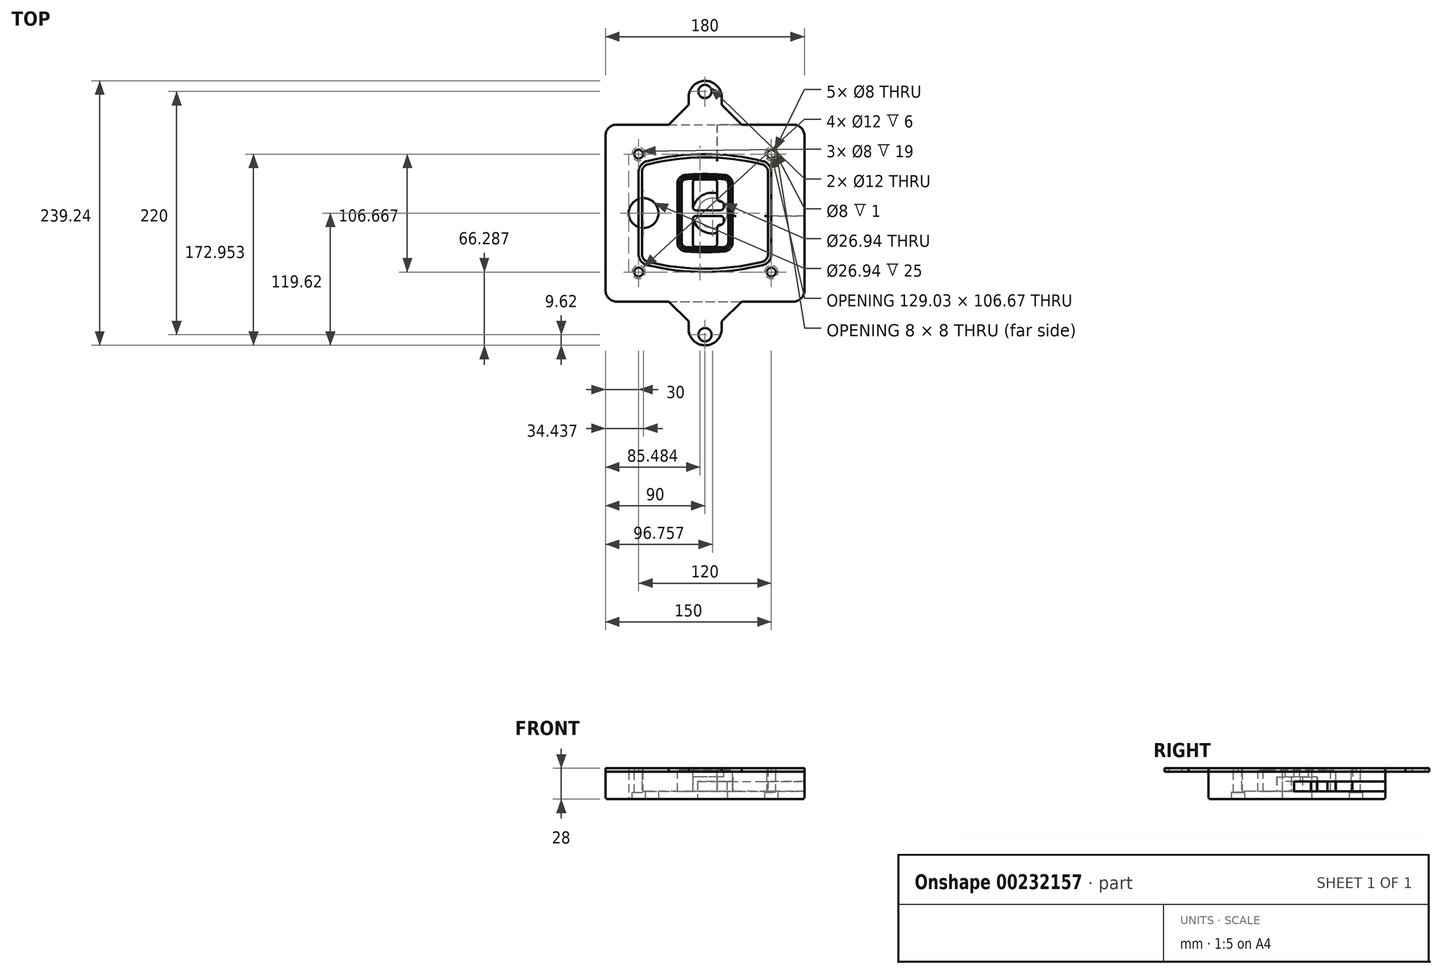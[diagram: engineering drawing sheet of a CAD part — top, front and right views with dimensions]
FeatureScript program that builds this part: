
annotation { "Feature Type Name" : "Feature", "Feature Type Description" : "" }
export const myFeature = defineFeature(function(context is Context, id is Id, definition is map)
    precondition{}
    {
        {
            var Q0;
            Q0=qCreatedBy(makeId("Top.planeOp"),FACE);
            var sketch = newSketch(context, id + "F0", { "sketchPlane" : qUnion([Q0])});
            skPoint(sketch, "E0.rect.middle", {"position": v(0, 0) * mm});
            skLineSegment(sketch, "E1.bottom", {"start": v(-80, -80) * mm, "end": v(80, -80) * mm});
            skLineSegment(sketch, "E1.top", {"start": v(-80, 80) * mm, "end": v(80, 80) * mm});
            skLineSegment(sketch, "E1.left", {"start": v(-90, -70) * mm, "end": v(-90, 70) * mm});
            skLineSegment(sketch, "E1.right", {"start": v(90, -70) * mm, "end": v(90, 70) * mm});
            skLineSegment(sketch, "E2", {"start": v(-90, 80) * mm, "end": v(90, -80) * mm, "construction": true});
            skLineSegment(sketch, "E3", {"start": v(90, 80) * mm, "end": v(-90, -80) * mm, "construction": true});
            skCircle(sketch, "E4", {"center": v(-60, 53.33) * mm, "radius": 4 * mm});
            skCircle(sketch, "E5", {"center": v(60, 53.33) * mm, "radius": 4 * mm});
            skCircle(sketch, "E6", {"center": v(60, -53.33) * mm, "radius": 4 * mm});
            skCircle(sketch, "E7", {"center": v(-60, -53.33) * mm, "radius": 4 * mm});
            skLineSegment(sketch, "E8", {"start": v(-60, 53.33) * mm, "end": v(60, 53.33) * mm, "construction": true});
            skLineSegment(sketch, "E9", {"start": v(60, 53.33) * mm, "end": v(60, -53.33) * mm, "construction": true});
            skLineSegment(sketch, "E10", {"start": v(60, -53.33) * mm, "end": v(-60, -53.33) * mm, "construction": true});
            skLineSegment(sketch, "E11", {"start": v(-60, -53.33) * mm, "end": v(-60, 53.33) * mm, "construction": true});
            skLineSegment(sketch, "E12", {"start": v(-60, 37.3) * mm, "end": v(-60, -37.3) * mm});
            skLineSegment(sketch, "E13", {"start": v(60, 37.3) * mm, "end": v(60, -37.3) * mm});
            skArc(sketch, "E14", {"start": v(52.38, 47.01) * mm, "mid": v(0, 53.33) * mm, "end": v(-52.38, 47.01) * mm});
            skArc(sketch, "E15", {"start": v(-52.38, -47.01) * mm, "mid": v(0, -53.33) * mm, "end": v(52.38, -47.01) * mm});
            skLineSegment(sketch, "E16", {"start": v(-60, 0) * mm, "end": v(60, 0) * mm, "construction": true});
            skPoint(sketch, "E17.visualSharp", {"position": v(-60, -45) * mm});
            skArc(sketch, "E17.filletArc", {"start": v(-60, -37.3) * mm, "mid": v(-57.87, -43.47) * mm, "end": v(-52.38, -47.01) * mm});
            skPoint(sketch, "E18.visualSharp", {"position": v(-60, 45) * mm});
            skArc(sketch, "E18.filletArc", {"start": v(-52.38, 47.01) * mm, "mid": v(-57.87, 43.47) * mm, "end": v(-60, 37.3) * mm});
            skPoint(sketch, "E19.visualSharp", {"position": v(60, 45) * mm});
            skArc(sketch, "E19.filletArc", {"start": v(60, 37.3) * mm, "mid": v(57.87, 43.47) * mm, "end": v(52.38, 47.01) * mm});
            skPoint(sketch, "E20.visualSharp", {"position": v(60, -45) * mm});
            skArc(sketch, "E20.filletArc", {"start": v(52.38, -47.01) * mm, "mid": v(57.87, -43.47) * mm, "end": v(60, -37.3) * mm});
            skPoint(sketch, "E21.visualSharp", {"position": v(-90, 80) * mm});
            skArc(sketch, "E21.filletArc", {"start": v(-80, 80) * mm, "mid": v(-87.07, 77.07) * mm, "end": v(-90, 70) * mm});
            skPoint(sketch, "E22.visualSharp", {"position": v(90, 80) * mm});
            skArc(sketch, "E22.filletArc", {"start": v(90, 70) * mm, "mid": v(87.07, 77.07) * mm, "end": v(80, 80) * mm});
            skPoint(sketch, "E23.visualSharp", {"position": v(90, -80) * mm});
            skArc(sketch, "E23.filletArc", {"start": v(80, -80) * mm, "mid": v(87.07, -77.07) * mm, "end": v(90, -70) * mm});
            skPoint(sketch, "E24.visualSharp", {"position": v(-90, -80) * mm});
            skArc(sketch, "E24.filletArc", {"start": v(-90, -70) * mm, "mid": v(-87.07, -77.07) * mm, "end": v(-80, -80) * mm});
            skArc(sketch, "E25.0", {"start": v(57, 37.3) * mm, "mid": v(55.5, 41.62) * mm, "end": v(51.67, 44.1) * mm});
            skLineSegment(sketch, "E25.1", {"start": v(57, 37.3) * mm, "end": v(57, -37.3) * mm});
            skArc(sketch, "E25.2", {"start": v(51.67, -44.1) * mm, "mid": v(55.5, -41.62) * mm, "end": v(57, -37.3) * mm});
            skArc(sketch, "E25.3", {"start": v(-51.67, -44.1) * mm, "mid": v(0, -50.33) * mm, "end": v(51.67, -44.1) * mm});
            skArc(sketch, "E25.4", {"start": v(-57, -37.3) * mm, "mid": v(-55.5, -41.62) * mm, "end": v(-51.67, -44.1) * mm});
            skArc(sketch, "E25.5", {"start": v(51.67, 44.1) * mm, "mid": v(0, 50.33) * mm, "end": v(-51.67, 44.1) * mm});
            skLineSegment(sketch, "E25.6", {"start": v(-57, 37.3) * mm, "end": v(-57, -37.3) * mm});
            skArc(sketch, "E25.7", {"start": v(-51.67, 44.1) * mm, "mid": v(-55.5, 41.62) * mm, "end": v(-57, 37.3) * mm});
            skArc(sketch, "E26.0", {"start": v(-53.33, 50.9) * mm, "mid": v(-61.01, 45.94) * mm, "end": v(-64, 37.3) * mm});
            skArc(sketch, "E26.1", {"start": v(53.33, 50.9) * mm, "mid": v(0, 57.33) * mm, "end": v(-53.33, 50.9) * mm});
            skArc(sketch, "E26.2", {"start": v(64, 37.3) * mm, "mid": v(61.01, 45.94) * mm, "end": v(53.33, 50.9) * mm});
            skLineSegment(sketch, "E26.3", {"start": v(64, 37.3) * mm, "end": v(64, -37.3) * mm});
            skArc(sketch, "E26.4", {"start": v(53.33, -50.9) * mm, "mid": v(61.01, -45.94) * mm, "end": v(64, -37.3) * mm});
            skLineSegment(sketch, "E26.5", {"start": v(-64, 37.3) * mm, "end": v(-64, -37.3) * mm});
            skArc(sketch, "E26.6", {"start": v(-53.33, -50.9) * mm, "mid": v(0, -57.33) * mm, "end": v(53.33, -50.9) * mm});
            skArc(sketch, "E26.7", {"start": v(-64, -37.3) * mm, "mid": v(-61.01, -45.94) * mm, "end": v(-53.33, -50.9) * mm});
            skSolve(sketch);
        }
        {
            var Q0;
            Q0=makeQuery(id+"F0.imprint","IMPRINT",FACE,{"disambiguationData":[TD([[makeQuery(id+"F0.imprint","IMPRINT",EDGE,{"derivedFrom":sQuery(id+"F0.wireOp",EDGE,"E1.bottom")}),1.0]])]});
            var Q1;
            Q1=makeQuery(id+"F0.imprint","IMPRINT",FACE,{"disambiguationData":[TD([[makeQuery(id+"F0.imprint","IMPRINT",EDGE,{"derivedFrom":sQuery(id+"F0.wireOp",EDGE,"E12")}),1.0]])]});
            var Q2;
            Q2=makeQuery(id+"F0.imprint","IMPRINT",FACE,{"disambiguationData":[TD([[makeQuery(id+"F0.imprint","IMPRINT",EDGE,{"derivedFrom":sQuery(id+"F0.wireOp",EDGE,"E25.0")}),1.0]])]});
            var Q3;
            Q3=makeQuery(id+"F0.imprint","IMPRINT",FACE,{"disambiguationData":[TD([[makeQuery(id+"F0.imprint","IMPRINT",EDGE,{"derivedFrom":sQuery(id+"F0.wireOp",EDGE,"E12")}),-1.0]])]});
            extrude(context, id + "F1", {"entities" : qUnion([Q0, Q1, Q2, Q3]), "oppositeDirection" : true, "depth" : 25 * mm});
        }
        {
            var Q0;
            Q0=makeQuery(id+"F0.imprint","IMPRINT",FACE,{"disambiguationData":[TD([[makeQuery(id+"F0.imprint","IMPRINT",EDGE,{"derivedFrom":sQuery(id+"F0.wireOp",EDGE,"E12")}),1.0]])]});
            extrude(context, id + "F2", {"entities" : qUnion([Q0]), "operationType" : NewBodyOperationType.ADD, "depth" : 3 * mm});
        }
        {
            var Q0;
            Q0=makeQuery(id+"F0.imprint","IMPRINT",FACE,{"disambiguationData":[TD([[makeQuery(id+"F0.imprint","IMPRINT",EDGE,{"derivedFrom":sQuery(id+"F0.wireOp",EDGE,"E25.0")}),1.0]])]});
            extrude(context, id + "F3", {"entities" : qUnion([Q0]), "operationType" : NewBodyOperationType.REMOVE, "oppositeDirection" : true, "depth" : 18 * mm});
        }
        {
            var Q0;
            Q0=makeQuery(id+"F2.opExtrude","CAP_FACE",FACE,{"disambiguationData":[OSD([sQuery(id+"F0.wireOp",EDGE,"E12"),sQuery(id+"F0.wireOp",EDGE,"E13"),sQuery(id+"F0.wireOp",EDGE,"E14"),sQuery(id+"F0.wireOp",EDGE,"E15"),sQuery(id+"F0.wireOp",EDGE,"E17.filletArc"),sQuery(id+"F0.wireOp",EDGE,"E18.filletArc"),sQuery(id+"F0.wireOp",EDGE,"E19.filletArc"),sQuery(id+"F0.wireOp",EDGE,"E20.filletArc"),sQuery(id+"F0.wireOp",EDGE,"E25.0"),sQuery(id+"F0.wireOp",EDGE,"E25.1"),sQuery(id+"F0.wireOp",EDGE,"E25.2"),sQuery(id+"F0.wireOp",EDGE,"E25.3"),sQuery(id+"F0.wireOp",EDGE,"E25.4"),sQuery(id+"F0.wireOp",EDGE,"E25.5"),sQuery(id+"F0.wireOp",EDGE,"E25.6"),sQuery(id+"F0.wireOp",EDGE,"E25.7")])],"isStart":false});
            var sketch = newSketch(context, id + "F4", { "sketchPlane" : qUnion([Q0])});
            skArc(sketch, "E27.0", {"start": v(-17.7, -34.56) * mm, "mid": v(0, -35.33) * mm, "end": v(17.7, -34.56) * mm});
            skArc(sketch, "E28.0", {"start": v(17.7, 34.56) * mm, "mid": v(0, 35.33) * mm, "end": v(-17.7, 34.56) * mm});
            skLineSegment(sketch, "E29", {"start": v(-25, 26.59) * mm, "end": v(-25, -26.59) * mm});
            skLineSegment(sketch, "E30", {"start": v(25, 26.59) * mm, "end": v(25, -26.59) * mm});
            skLineSegment(sketch, "E31", {"start": v(-25, 33.78) * mm, "end": v(25, 33.78) * mm, "construction": true});
            skLineSegment(sketch, "E32", {"start": v(-25, -33.78) * mm, "end": v(25, -33.78) * mm, "construction": true});
            skPoint(sketch, "E33.visualSharp", {"position": v(-25, 33.78) * mm});
            skArc(sketch, "E33.filletArc", {"start": v(-17.7, 34.56) * mm, "mid": v(-22.9, 32) * mm, "end": v(-25, 26.59) * mm});
            skPoint(sketch, "E34.visualSharp", {"position": v(25, 33.78) * mm});
            skArc(sketch, "E34.filletArc", {"start": v(25, 26.59) * mm, "mid": v(22.9, 32) * mm, "end": v(17.7, 34.56) * mm});
            skPoint(sketch, "E35.visualSharp", {"position": v(25, -33.78) * mm});
            skArc(sketch, "E35.filletArc", {"start": v(17.7, -34.56) * mm, "mid": v(22.9, -32) * mm, "end": v(25, -26.59) * mm});
            skPoint(sketch, "E36.visualSharp", {"position": v(-25, -33.78) * mm});
            skArc(sketch, "E36.filletArc", {"start": v(-25, -26.59) * mm, "mid": v(-22.9, -32) * mm, "end": v(-17.7, -34.56) * mm});
            skArc(sketch, "E37.0", {"start": v(51.67, 44.1) * mm, "mid": v(0, 50.33) * mm, "end": v(-51.67, 44.1) * mm});
            skArc(sketch, "E37.1", {"start": v(-51.67, 44.1) * mm, "mid": v(-55.5, 41.62) * mm, "end": v(-57, 37.3) * mm});
            skLineSegment(sketch, "E37.2", {"start": v(-57, 37.3) * mm, "end": v(-57, -37.3) * mm});
            skArc(sketch, "E37.3", {"start": v(-57, -37.3) * mm, "mid": v(-55.5, -41.62) * mm, "end": v(-51.67, -44.1) * mm});
            skArc(sketch, "E37.4", {"start": v(-51.67, -44.1) * mm, "mid": v(0, -50.33) * mm, "end": v(51.67, -44.1) * mm});
            skArc(sketch, "E37.5", {"start": v(51.67, -44.1) * mm, "mid": v(55.5, -41.62) * mm, "end": v(57, -37.3) * mm});
            skLineSegment(sketch, "E37.6", {"start": v(57, 37.3) * mm, "end": v(57, -37.3) * mm});
            skArc(sketch, "E37.7", {"start": v(57, 37.3) * mm, "mid": v(55.5, 41.62) * mm, "end": v(51.67, 44.1) * mm});
            skLineSegment(sketch, "E38.0", {"start": v(23, 26.59) * mm, "end": v(23, -26.59) * mm});
            skArc(sketch, "E38.1", {"start": v(17.53, -32.56) * mm, "mid": v(21.42, -30.64) * mm, "end": v(23, -26.59) * mm});
            skArc(sketch, "E38.2", {"start": v(-17.53, -32.56) * mm, "mid": v(0, -33.33) * mm, "end": v(17.53, -32.56) * mm});
            skArc(sketch, "E38.3", {"start": v(-23, -26.59) * mm, "mid": v(-21.42, -30.64) * mm, "end": v(-17.53, -32.56) * mm});
            skLineSegment(sketch, "E38.4", {"start": v(-23, 26.59) * mm, "end": v(-23, -26.59) * mm});
            skArc(sketch, "E38.5", {"start": v(23, 26.59) * mm, "mid": v(21.42, 30.64) * mm, "end": v(17.53, 32.56) * mm});
            skArc(sketch, "E38.6", {"start": v(-17.53, 32.56) * mm, "mid": v(-21.42, 30.64) * mm, "end": v(-23, 26.59) * mm});
            skArc(sketch, "E38.7", {"start": v(17.53, 32.56) * mm, "mid": v(0, 33.33) * mm, "end": v(-17.53, 32.56) * mm});
            skArc(sketch, "E39.0", {"start": v(21, 26.59) * mm, "mid": v(19.95, 29.29) * mm, "end": v(17.35, 30.57) * mm});
            skLineSegment(sketch, "E39.1", {"start": v(21, 26.59) * mm, "end": v(21, -26.59) * mm});
            skArc(sketch, "E39.2", {"start": v(17.35, -30.57) * mm, "mid": v(19.95, -29.29) * mm, "end": v(21, -26.59) * mm});
            skArc(sketch, "E39.3", {"start": v(-17.35, -30.57) * mm, "mid": v(0, -31.33) * mm, "end": v(17.35, -30.57) * mm});
            skArc(sketch, "E39.4", {"start": v(-21, -26.59) * mm, "mid": v(-19.95, -29.29) * mm, "end": v(-17.35, -30.57) * mm});
            skArc(sketch, "E39.5", {"start": v(17.35, 30.57) * mm, "mid": v(0, 31.33) * mm, "end": v(-17.35, 30.57) * mm});
            skLineSegment(sketch, "E39.6", {"start": v(-21, 26.59) * mm, "end": v(-21, -26.59) * mm});
            skArc(sketch, "E39.7", {"start": v(-17.35, 30.57) * mm, "mid": v(-19.95, 29.29) * mm, "end": v(-21, 26.59) * mm});
            skLineSegment(sketch, "E40", {"start": v(-25, 0) * mm, "end": v(25, 0) * mm, "construction": true});
            skLineSegment(sketch, "E41", {"start": v(-11, 5.5) * mm, "end": v(-11, 27.5) * mm});
            skLineSegment(sketch, "E42", {"start": v(-8, 30.5) * mm, "end": v(8, 30.5) * mm});
            skLineSegment(sketch, "E43", {"start": v(11, 27.5) * mm, "end": v(11, 13.5) * mm});
            skLineSegment(sketch, "E44", {"start": v(14, 10.5) * mm, "end": v(14, 10.5) * mm});
            skLineSegment(sketch, "E45", {"start": v(17, 7.5) * mm, "end": v(17, 5.5) * mm});
            skLineSegment(sketch, "E46", {"start": v(14, 2.5) * mm, "end": v(-8, 2.5) * mm});
            skPoint(sketch, "E47.visualSharp", {"position": v(-11, 30.5) * mm});
            skArc(sketch, "E47.filletArc", {"start": v(-8, 30.5) * mm, "mid": v(-10.12, 29.62) * mm, "end": v(-11, 27.5) * mm});
            skPoint(sketch, "E48.visualSharp", {"position": v(11, 30.5) * mm});
            skArc(sketch, "E48.filletArc", {"start": v(11, 27.5) * mm, "mid": v(10.12, 29.62) * mm, "end": v(8, 30.5) * mm});
            skPoint(sketch, "E49.visualSharp", {"position": v(11, 10.5) * mm});
            skArc(sketch, "E49.filletArc", {"start": v(11, 13.5) * mm, "mid": v(11.88, 11.38) * mm, "end": v(14, 10.5) * mm});
            skPoint(sketch, "E50.visualSharp", {"position": v(17, 10.5) * mm});
            skArc(sketch, "E50.filletArc", {"start": v(17, 7.5) * mm, "mid": v(16.12, 9.62) * mm, "end": v(14, 10.5) * mm});
            skPoint(sketch, "E51.visualSharp", {"position": v(17, 2.5) * mm});
            skArc(sketch, "E51.filletArc", {"start": v(14, 2.5) * mm, "mid": v(16.12, 3.38) * mm, "end": v(17, 5.5) * mm});
            skPoint(sketch, "E52.visualSharp", {"position": v(-11, 2.5) * mm});
            skArc(sketch, "E52.filletArc", {"start": v(-11, 5.5) * mm, "mid": v(-10.12, 3.38) * mm, "end": v(-8, 2.5) * mm});
            skLineSegment(sketch, "E53.0.MirrorCS", {"start": v(14, -2.5) * mm, "end": v(-8, -2.5) * mm});
            skArc(sketch, "E54.0.MirrorCS", {"start": v(-11, -5.5) * mm, "mid": v(-10.12, -3.38) * mm, "end": v(-8, -2.5) * mm});
            skLineSegment(sketch, "E55.0.MirrorCS", {"start": v(-11, -5.5) * mm, "end": v(-11, -27.5) * mm});
            skArc(sketch, "E56.0.MirrorCS", {"start": v(-8, -30.5) * mm, "mid": v(-10.12, -29.62) * mm, "end": v(-11, -27.5) * mm});
            skLineSegment(sketch, "E57.0.MirrorCS", {"start": v(-8, -30.5) * mm, "end": v(8, -30.5) * mm});
            skArc(sketch, "E58.0.MirrorCS", {"start": v(11, -27.5) * mm, "mid": v(10.12, -29.62) * mm, "end": v(8, -30.5) * mm});
            skLineSegment(sketch, "E59.0.MirrorCS", {"start": v(11, -27.5) * mm, "end": v(11, -13.5) * mm});
            skArc(sketch, "E60.0.MirrorCS", {"start": v(11, -13.5) * mm, "mid": v(11.88, -11.38) * mm, "end": v(14, -10.5) * mm});
            skArc(sketch, "E61.0.MirrorCS", {"start": v(17, -7.5) * mm, "mid": v(16.12, -9.62) * mm, "end": v(14, -10.5) * mm});
            skLineSegment(sketch, "E62.0.MirrorCS", {"start": v(17, -7.5) * mm, "end": v(17, -5.5) * mm});
            skArc(sketch, "E63.0.MirrorCS", {"start": v(14, -2.5) * mm, "mid": v(16.12, -3.38) * mm, "end": v(17, -5.5) * mm});
            skSolve(sketch);
        }
        {
            var Q0;
            Q0=makeQuery(id+"F4.imprint","IMPRINT",FACE,{"disambiguationData":[TD([[makeQuery(id+"F4.imprint","IMPRINT",EDGE,{"derivedFrom":sQuery(id+"F4.wireOp",EDGE,"E27.0")}),1.0]])]});
            var Q1;
            Q1=makeQuery(id+"F4.imprint","IMPRINT",FACE,{"disambiguationData":[TD([[makeQuery(id+"F4.imprint","IMPRINT",EDGE,{"derivedFrom":sQuery(id+"F4.wireOp",EDGE,"E38.0")}),-1.0]])]});
            var Q2;
            Q2=makeQuery(id+"F4.imprint","IMPRINT",FACE,{"disambiguationData":[TD([[makeQuery(id+"F4.imprint","IMPRINT",EDGE,{"derivedFrom":sQuery(id+"F4.wireOp",EDGE,"E39.0")}),1.0]])]});
            extrude(context, id + "F5", {"entities" : qUnion([Q0, Q1, Q2]), "operationType" : NewBodyOperationType.ADD, "endBound" : BoundingType.UP_TO_NEXT, "oppositeDirection" : true, "depth" : 25 * mm});
        }
        {
            var Q0;
            Q0=makeQuery(id+"F4.imprint","IMPRINT",FACE,{"disambiguationData":[TD([[makeQuery(id+"F4.imprint","IMPRINT",EDGE,{"derivedFrom":sQuery(id+"F4.wireOp",EDGE,"E38.0")}),-1.0]])]});
            extrude(context, id + "F6", {"entities" : qUnion([Q0]), "operationType" : NewBodyOperationType.REMOVE, "oppositeDirection" : true, "depth" : 2 * mm});
        }
        {
            var Q0;
            Q0=makeQuery(id+"F1.opExtrude","CAP_FACE",FACE,{"disambiguationData":[OSD([sQuery(id+"F0.wireOp",EDGE,"E1.bottom"),sQuery(id+"F0.wireOp",EDGE,"E1.top"),sQuery(id+"F0.wireOp",EDGE,"E1.left"),sQuery(id+"F0.wireOp",EDGE,"E1.right"),sQuery(id+"F0.wireOp",EDGE,"E4"),sQuery(id+"F0.wireOp",EDGE,"E5"),sQuery(id+"F0.wireOp",EDGE,"E6"),sQuery(id+"F0.wireOp",EDGE,"E7"),sQuery(id+"F0.wireOp",EDGE,"E21.filletArc"),sQuery(id+"F0.wireOp",EDGE,"E22.filletArc"),sQuery(id+"F0.wireOp",EDGE,"E23.filletArc"),sQuery(id+"F0.wireOp",EDGE,"E24.filletArc")])],"isStart":false});
            var sketch = newSketch(context, id + "F7", { "sketchPlane" : qUnion([Q0])});
            skCircle(sketch, "E64", {"center": v(6.76, 0) * mm, "radius": 13.47 * mm});
            skCircle(sketch, "E65", {"center": v(-55.56, 0) * mm, "radius": 13.47 * mm});
            skLineSegment(sketch, "E66", {"start": v(90, 0) * mm, "end": v(-90, 0) * mm});
            skCircle(sketch, "E67", {"center": v(6.76, 0) * mm, "radius": 18.47 * mm});
            skCircle(sketch, "E68", {"center": v(60, -53.33) * mm, "radius": 6 * mm});
            skCircle(sketch, "E69", {"center": v(-60, -53.33) * mm, "radius": 6 * mm});
            skCircle(sketch, "E70", {"center": v(-60, 53.33) * mm, "radius": 6 * mm});
            skCircle(sketch, "E71", {"center": v(60, 53.33) * mm, "radius": 6 * mm});
            skSolve(sketch);
        }
        {
            var Q0;
            {var subQ1=sQuery(id+"F7.wireOp",EDGE,"E66");var subQ4=sQuery(id+"F7.wireOp",EDGE,"E64");var subQ6=makeQuery(id+"F7.imprint","INTERSECT",VERTEX,{"disambiguationData":[OD(0.0)],"derivedFrom":[subQ4,subQ1]});Q0=makeQuery(id+"F7.imprint","IMPRINT",FACE,{"disambiguationData":[TD([[makeQuery(id+"F7.imprint","IMPRINT",EDGE,{"disambiguationData":[TD([[subQ6,-1.0]])],"derivedFrom":subQ4}),-1.0]])]});}
            var Q1;
            {var subQ0=sQuery(id+"F7.wireOp",EDGE,"E66");var subQ1=sQuery(id+"F7.wireOp",EDGE,"E64");var subQ3=makeQuery(id+"F7.imprint","INTERSECT",VERTEX,{"disambiguationData":[OD(0.0)],"derivedFrom":[subQ1,subQ0]});Q1=makeQuery(id+"F7.imprint","IMPRINT",FACE,{"disambiguationData":[TD([[makeQuery(id+"F7.imprint","IMPRINT",EDGE,{"disambiguationData":[TD([[subQ3,-1.0]])],"derivedFrom":subQ1}),1.0]])]});}
            var Q2;
            {var subQ0=sQuery(id+"F7.wireOp",EDGE,"E66");var subQ1=sQuery(id+"F7.wireOp",EDGE,"E64");var subQ3=makeQuery(id+"F7.imprint","INTERSECT",VERTEX,{"disambiguationData":[OD(0.0)],"derivedFrom":[subQ1,subQ0]});Q2=makeQuery(id+"F7.imprint","IMPRINT",FACE,{"disambiguationData":[TD([[makeQuery(id+"F7.imprint","IMPRINT",EDGE,{"disambiguationData":[TD([[subQ3,1.0]])],"derivedFrom":subQ1}),1.0]])]});}
            var Q3;
            {var subQ1=sQuery(id+"F7.wireOp",EDGE,"E66");var subQ4=sQuery(id+"F7.wireOp",EDGE,"E64");var subQ6=makeQuery(id+"F7.imprint","INTERSECT",VERTEX,{"disambiguationData":[OD(0.0)],"derivedFrom":[subQ4,subQ1]});Q3=makeQuery(id+"F7.imprint","IMPRINT",FACE,{"disambiguationData":[TD([[makeQuery(id+"F7.imprint","IMPRINT",EDGE,{"disambiguationData":[TD([[subQ6,1.0]])],"derivedFrom":subQ4}),-1.0]])]});}
            extrude(context, id + "F8", {"entities" : qUnion([Q0, Q1, Q2, Q3]), "operationType" : NewBodyOperationType.ADD, "oppositeDirection" : true, "depth" : 20 * mm});
        }
        {
            var Q0;
            {var subQ0=sQuery(id+"F7.wireOp",EDGE,"E66");var subQ1=sQuery(id+"F7.wireOp",EDGE,"E64");var subQ3=makeQuery(id+"F7.imprint","INTERSECT",VERTEX,{"disambiguationData":[OD(0.0)],"derivedFrom":[subQ1,subQ0]});Q0=makeQuery(id+"F7.imprint","IMPRINT",FACE,{"disambiguationData":[TD([[makeQuery(id+"F7.imprint","IMPRINT",EDGE,{"disambiguationData":[TD([[subQ3,-1.0]])],"derivedFrom":subQ1}),1.0]])]});}
            var Q1;
            {var subQ0=sQuery(id+"F7.wireOp",EDGE,"E66");var subQ1=sQuery(id+"F7.wireOp",EDGE,"E64");var subQ3=makeQuery(id+"F7.imprint","INTERSECT",VERTEX,{"disambiguationData":[OD(0.0)],"derivedFrom":[subQ1,subQ0]});Q1=makeQuery(id+"F7.imprint","IMPRINT",FACE,{"disambiguationData":[TD([[makeQuery(id+"F7.imprint","IMPRINT",EDGE,{"disambiguationData":[TD([[subQ3,1.0]])],"derivedFrom":subQ1}),1.0]])]});}
            extrude(context, id + "F9", {"entities" : qUnion([Q0, Q1]), "operationType" : NewBodyOperationType.REMOVE, "oppositeDirection" : true, "depth" : 16 * mm});
        }
        {
            var Q0;
            {var subQ0=sQuery(id+"F7.wireOp",EDGE,"E66");var subQ1=sQuery(id+"F7.wireOp",EDGE,"E65");var subQ3=makeQuery(id+"F7.imprint","INTERSECT",VERTEX,{"disambiguationData":[OD(0.0)],"derivedFrom":[subQ1,subQ0]});Q0=makeQuery(id+"F7.imprint","IMPRINT",FACE,{"disambiguationData":[TD([[makeQuery(id+"F7.imprint","IMPRINT",EDGE,{"disambiguationData":[TD([[subQ3,-1.0]])],"derivedFrom":subQ1}),1.0]])]});}
            var Q1;
            {var subQ0=sQuery(id+"F7.wireOp",EDGE,"E66");var subQ1=sQuery(id+"F7.wireOp",EDGE,"E65");var subQ3=makeQuery(id+"F7.imprint","INTERSECT",VERTEX,{"disambiguationData":[OD(0.0)],"derivedFrom":[subQ1,subQ0]});Q1=makeQuery(id+"F7.imprint","IMPRINT",FACE,{"disambiguationData":[TD([[makeQuery(id+"F7.imprint","IMPRINT",EDGE,{"disambiguationData":[TD([[subQ3,1.0]])],"derivedFrom":subQ1}),1.0]])]});}
            extrude(context, id + "F10", {"entities" : qUnion([Q0, Q1]), "operationType" : NewBodyOperationType.REMOVE, "oppositeDirection" : true, "depth" : 25 * mm});
        }
        {
            var Q0;
            Q0=makeQuery(id+"F7.imprint","IMPRINT",FACE,{"disambiguationData":[TD([[makeQuery(id+"F7.imprint","IMPRINT",EDGE,{"derivedFrom":sQuery(id+"F7.wireOp",EDGE,"E68")}),1.0]])]});
            var Q1;
            Q1=makeQuery(id+"F7.imprint","IMPRINT",FACE,{"disambiguationData":[TD([[makeQuery(id+"F7.imprint","IMPRINT",EDGE,{"derivedFrom":makeQuery(id+"F1.opExtrude","CAP_EDGE",EDGE,{"disambiguationData":[OSD([sQuery(id+"F0.wireOp",EDGE,"E5")])],"isStart":false})}),-1.0]])]});
            var Q2;
            Q2=makeQuery(id+"F7.imprint","IMPRINT",FACE,{"disambiguationData":[TD([[makeQuery(id+"F7.imprint","IMPRINT",EDGE,{"derivedFrom":sQuery(id+"F7.wireOp",EDGE,"E69")}),1.0]])]});
            var Q3;
            Q3=makeQuery(id+"F7.imprint","IMPRINT",FACE,{"disambiguationData":[TD([[makeQuery(id+"F7.imprint","IMPRINT",EDGE,{"derivedFrom":makeQuery(id+"F1.opExtrude","CAP_EDGE",EDGE,{"disambiguationData":[OSD([sQuery(id+"F0.wireOp",EDGE,"E4")])],"isStart":false})}),-1.0]])]});
            var Q4;
            Q4=makeQuery(id+"F7.imprint","IMPRINT",FACE,{"disambiguationData":[TD([[makeQuery(id+"F7.imprint","IMPRINT",EDGE,{"derivedFrom":sQuery(id+"F7.wireOp",EDGE,"E70")}),1.0]])]});
            var Q5;
            Q5=makeQuery(id+"F7.imprint","IMPRINT",FACE,{"disambiguationData":[TD([[makeQuery(id+"F7.imprint","IMPRINT",EDGE,{"derivedFrom":makeQuery(id+"F1.opExtrude","CAP_EDGE",EDGE,{"disambiguationData":[OSD([sQuery(id+"F0.wireOp",EDGE,"E7")])],"isStart":false})}),-1.0]])]});
            var Q6;
            Q6=makeQuery(id+"F7.imprint","IMPRINT",FACE,{"disambiguationData":[TD([[makeQuery(id+"F7.imprint","IMPRINT",EDGE,{"derivedFrom":sQuery(id+"F7.wireOp",EDGE,"E71")}),1.0]])]});
            var Q7;
            Q7=makeQuery(id+"F7.imprint","IMPRINT",FACE,{"disambiguationData":[TD([[makeQuery(id+"F7.imprint","IMPRINT",EDGE,{"derivedFrom":makeQuery(id+"F1.opExtrude","CAP_EDGE",EDGE,{"disambiguationData":[OSD([sQuery(id+"F0.wireOp",EDGE,"E6")])],"isStart":false})}),-1.0]])]});
            extrude(context, id + "F11", {"entities" : qUnion([Q0, Q1, Q2, Q3, Q4, Q5, Q6, Q7]), "operationType" : NewBodyOperationType.REMOVE, "oppositeDirection" : true, "depth" : 6 * mm});
        }
        {
            var Q0;
            Q0=makeQuery(id+"F9.boolean.opBoolean","COPY",FACE,{"derivedFrom":makeQuery(id+"F9.opExtrude","CAP_FACE",FACE,{"disambiguationData":[OSD([sQuery(id+"F7.wireOp",EDGE,"E64")])],"isStart":false})});
            var sketch = newSketch(context, id + "F12", { "sketchPlane" : qUnion([Q0])});
            skArc(sketch, "E72.0", {"start": v(11, -88.19) * mm, "mid": v(97.1, -83.6) * mm, "end": v(92.5, 2.5) * mm});
            skLineSegment(sketch, "E72.1", {"start": v(11, -17.97) * mm, "end": v(11, -17.97) * mm});
            skLineSegment(sketch, "E73", {"start": v(92.5, -105.13) * mm, "end": v(102.3, -105.13) * mm});
            skLineSegment(sketch, "E74.0", {"start": v(92.5, 2.5) * mm, "end": v(14, 2.5) * mm});
            skArc(sketch, "E74.1", {"start": v(14, 2.5) * mm, "mid": v(16.12, 3.38) * mm, "end": v(17, 5.5) * mm});
            skLineSegment(sketch, "E74.2", {"start": v(17, 7.5) * mm, "end": v(17, 5.5) * mm});
            skArc(sketch, "E74.3", {"start": v(17, 7.5) * mm, "mid": v(16.12, 9.62) * mm, "end": v(14, 10.5) * mm});
            skArc(sketch, "E74.4", {"start": v(11, 13.5) * mm, "mid": v(11.88, 11.38) * mm, "end": v(14, 10.5) * mm});
            skLineSegment(sketch, "E74.5", {"start": v(11, 13.5) * mm, "end": v(11, -88.19) * mm});
            skLineSegment(sketch, "E74.7", {"start": v(92.5, -2.5) * mm, "end": v(14, -2.5) * mm});
            skArc(sketch, "E74.8", {"start": v(14, -2.5) * mm, "mid": v(16.12, -3.38) * mm, "end": v(17, -5.5) * mm});
            skLineSegment(sketch, "E74.9", {"start": v(17, -7.5) * mm, "end": v(17, -5.5) * mm});
            skArc(sketch, "E74.10", {"start": v(17, -7.5) * mm, "mid": v(16.12, -9.62) * mm, "end": v(14, -10.5) * mm});
            skArc(sketch, "E74.11", {"start": v(11, -13.5) * mm, "mid": v(11.88, -11.38) * mm, "end": v(14, -10.5) * mm});
            skLineSegment(sketch, "E74.12", {"start": v(11, -17.97) * mm, "end": v(11, -13.5) * mm});
            skPoint(sketch, "E75.orphan", {"position": v(11, -27.5) * mm});
            skPoint(sketch, "E76.orphan", {"position": v(-8, -2.5) * mm});
            skPoint(sketch, "E77.orphan", {"position": v(-8, 2.5) * mm});
            skPoint(sketch, "E78.orphan", {"position": v(11, 27.5) * mm});
            skSolve(sketch);
        }
        {
            var Q0;
            {var subQ7=sQuery(id+"F12.wireOp",EDGE,"E72.0");var subQ14=sQuery(id+"F12.wireOp",EDGE,"E72.1");var subQ16=sQuery(id+"F12.wireOp",EDGE,"E74.1");var subQ18=sQuery(id+"F12.wireOp",EDGE,"E74.8");Q0=qUnion([makeQuery(id+"F12.imprint","IMPRINT",FACE,{"disambiguationData":[TD([[makeQuery(id+"F12.imprint","IMPRINT",EDGE,{"derivedFrom":subQ7}),1.0]])]}),makeQuery(id+"F12.imprint","IMPRINT",FACE,{"disambiguationData":[TD([[makeQuery(id+"F12.imprint","IMPRINT",EDGE,{"derivedFrom":subQ14}),1.0]])]}),makeQuery(id+"F12.imprint","IMPRINT",FACE,{"disambiguationData":[TD([[makeQuery(id+"F12.imprint","IMPRINT",EDGE,{"derivedFrom":subQ16}),1.0]])]}),makeQuery(id+"F12.imprint","IMPRINT",FACE,{"disambiguationData":[TD([[makeQuery(id+"F12.imprint","IMPRINT",EDGE,{"derivedFrom":subQ18}),-1.0]])]})]);}
            var Q1;
            Q1=makeQuery(id+"F5.boolean.opBoolean","SPLIT",FACE,{"disambiguationData":[TD([makeQuery(id+"F5.opExtrude","SWEPT_FACE",FACE,{"disambiguationData":[OSD([sQuery(id+"F4.wireOp",EDGE,"E41")])]})])],"derivedFrom":makeQuery(id+"F3.boolean.opBoolean","COPY",FACE,{"derivedFrom":makeQuery(id+"F3.opExtrude","CAP_FACE",FACE,{"disambiguationData":[OSD([sQuery(id+"F0.wireOp",EDGE,"E25.0"),sQuery(id+"F0.wireOp",EDGE,"E25.1"),sQuery(id+"F0.wireOp",EDGE,"E25.2"),sQuery(id+"F0.wireOp",EDGE,"E25.3"),sQuery(id+"F0.wireOp",EDGE,"E25.4"),sQuery(id+"F0.wireOp",EDGE,"E25.5"),sQuery(id+"F0.wireOp",EDGE,"E25.6"),sQuery(id+"F0.wireOp",EDGE,"E25.7")])],"isStart":false})})});
            extrude(context, id + "F13", {"entities" : qUnion([Q0]), "operationType" : NewBodyOperationType.REMOVE, "endBound" : BoundingType.UP_TO_SURFACE, "endBoundEntityFace" : qUnion([Q1]), "depth" : 25 * mm});
        }
        {
            var Q0;
            Q0=makeQuery(id+"F3.boolean.opBoolean","COPY",EDGE,{"derivedFrom":makeQuery(id+"F3.opExtrude","CAP_EDGE",EDGE,{"disambiguationData":[OSD([sQuery(id+"F0.wireOp",EDGE,"E25.6")])],"isStart":false})});
            var Q1;
            Q1=makeQuery(id+"F8.boolean.opBoolean","INTERSECT",EDGE,{"derivedFrom":[makeQuery(id+"F5.opExtrude","SWEPT_FACE",FACE,{"disambiguationData":[OSD([sQuery(id+"F4.wireOp",EDGE,"E30")])]}),makeQuery(id+"F8.opExtrude","CAP_FACE",FACE,{"disambiguationData":[OSD([sQuery(id+"F7.wireOp",EDGE,"E67")])],"isStart":false})]});
            var Q2;
            Q2=makeQuery(id+"F8.boolean.opBoolean","INTERSECT",EDGE,{"disambiguationData":[OD(1.0)],"derivedFrom":[makeQuery(id+"F5.opExtrude","SWEPT_FACE",FACE,{"disambiguationData":[OSD([sQuery(id+"F4.wireOp",EDGE,"E30")])]}),makeQuery(id+"F8.opExtrude","SWEPT_FACE",FACE,{"disambiguationData":[OSD([sQuery(id+"F7.wireOp",EDGE,"E67")])]})]});
            var Q3;
            {var subQ0=makeQuery(id+"F3.boolean.opBoolean","COPY",FACE,{"derivedFrom":makeQuery(id+"F3.opExtrude","CAP_FACE",FACE,{"disambiguationData":[OSD([sQuery(id+"F0.wireOp",EDGE,"E25.0"),sQuery(id+"F0.wireOp",EDGE,"E25.1"),sQuery(id+"F0.wireOp",EDGE,"E25.2"),sQuery(id+"F0.wireOp",EDGE,"E25.3"),sQuery(id+"F0.wireOp",EDGE,"E25.4"),sQuery(id+"F0.wireOp",EDGE,"E25.5"),sQuery(id+"F0.wireOp",EDGE,"E25.6"),sQuery(id+"F0.wireOp",EDGE,"E25.7")])],"isStart":false})});var subQ1=sQuery(id+"F4.wireOp",EDGE,"E30");Q3=makeQuery(id+"F8.boolean.opBoolean","SPLIT",EDGE,{"disambiguationData":[TD([makeQuery(id+"F5.opExtrude","SWEPT_FACE",FACE,{"disambiguationData":[OSD([sQuery(id+"F4.wireOp",EDGE,"E35.filletArc")])]})])],"derivedFrom":makeQuery(id+"F5.opExtrude","TWEAK_EDGE",EDGE,{"derivedFrom":[subQ0,makeQuery(id+"F4.imprint","IMPRINT",EDGE,{"derivedFrom":subQ1})]})});}
            var Q4;
            {var subQ0=sQuery(id+"F0.wireOp",EDGE,"E25.0");var subQ1=sQuery(id+"F0.wireOp",EDGE,"E25.1");var subQ2=sQuery(id+"F0.wireOp",EDGE,"E25.2");var subQ3=sQuery(id+"F0.wireOp",EDGE,"E25.3");var subQ4=sQuery(id+"F0.wireOp",EDGE,"E25.4");var subQ5=sQuery(id+"F0.wireOp",EDGE,"E25.5");var subQ6=sQuery(id+"F0.wireOp",EDGE,"E25.6");var subQ7=sQuery(id+"F0.wireOp",EDGE,"E25.7");Q4=makeQuery(id+"F8.boolean.opBoolean","INTERSECT",EDGE,{"derivedFrom":[makeQuery(id+"F5.boolean.opBoolean","SPLIT",FACE,{"disambiguationData":[TD([makeQuery(id+"F2.opExtrude","SWEPT_FACE",FACE,{"disambiguationData":[OSD([subQ0])]})])],"derivedFrom":makeQuery(id+"F3.boolean.opBoolean","COPY",FACE,{"derivedFrom":makeQuery(id+"F3.opExtrude","CAP_FACE",FACE,{"disambiguationData":[OSD([subQ0,subQ1,subQ2,subQ3,subQ4,subQ5,subQ6,subQ7])],"isStart":false})})}),makeQuery(id+"F8.opExtrude","SWEPT_FACE",FACE,{"disambiguationData":[OSD([sQuery(id+"F7.wireOp",EDGE,"E67")])]})]});}
            var Q5;
            Q5=makeQuery(id+"F8.boolean.opBoolean","INTERSECT",EDGE,{"disambiguationData":[OD(0.0)],"derivedFrom":[makeQuery(id+"F5.opExtrude","SWEPT_FACE",FACE,{"disambiguationData":[OSD([sQuery(id+"F4.wireOp",EDGE,"E30")])]}),makeQuery(id+"F8.opExtrude","SWEPT_FACE",FACE,{"disambiguationData":[OSD([sQuery(id+"F7.wireOp",EDGE,"E67")])]})]});
            fillet(context, id + "F14", {"entities" : qUnion([Q0, Q1, Q2, Q3, Q4, Q5]), "radius" : 3 * mm, "tangentPropagation" : true, "allowEdgeOverflow" : false});
        }
        {
            var Q0;
            Q0=makeQuery(id+"F1.opExtrude","CAP_EDGE",EDGE,{"disambiguationData":[OSD([sQuery(id+"F0.wireOp",EDGE,"E1.bottom")])],"isStart":false});
            fillet(context, id + "F15", {"entities" : qUnion([Q0]), "radius" : 2 * mm, "tangentPropagation" : true, "allowEdgeOverflow" : false});
        }
        {
            var Q0;
            {var subQ0=sQuery(id+"F0.wireOp",EDGE,"E22.filletArc");var subQ1=sQuery(id+"F0.wireOp",EDGE,"E7");var subQ2=sQuery(id+"F0.wireOp",EDGE,"E6");var subQ3=sQuery(id+"F0.wireOp",EDGE,"E5");var subQ4=sQuery(id+"F0.wireOp",EDGE,"E4");var subQ5=sQuery(id+"F0.wireOp",EDGE,"E1.bottom");var subQ6=sQuery(id+"F0.wireOp",EDGE,"E21.filletArc");var subQ7=sQuery(id+"F0.wireOp",EDGE,"E1.top");var subQ8=sQuery(id+"F0.wireOp",EDGE,"E1.left");var subQ9=sQuery(id+"F0.wireOp",EDGE,"E1.right");var subQ10=sQuery(id+"F0.wireOp",EDGE,"E23.filletArc");var subQ11=sQuery(id+"F0.wireOp",EDGE,"E24.filletArc");Q0=makeQuery(id+"F2.boolean.opBoolean","SPLIT",FACE,{"disambiguationData":[TD([makeQuery(id+"F1.opExtrude","SWEPT_FACE",FACE,{"disambiguationData":[OSD([subQ5])]})])],"derivedFrom":makeQuery(id+"F1.opExtrude","CAP_FACE",FACE,{"disambiguationData":[OSD([subQ5,subQ7,subQ8,subQ9,subQ4,subQ3,subQ2,subQ1,subQ6,subQ0,subQ10,subQ11])],"isStart":true})});}
            var sketch = newSketch(context, id + "F16", { "sketchPlane" : qUnion([Q0])});
            skLineSegment(sketch, "E79", {"start": v(-32.85, 80) * mm, "end": v(-14.85, 98) * mm});
            skLineSegment(sketch, "E80", {"start": v(33.15, 80) * mm, "end": v(15.15, 98) * mm});
            skLineSegment(sketch, "E81", {"start": v(-14.85, 98) * mm, "end": v(-14.85, 104.33) * mm});
            skLineSegment(sketch, "E82", {"start": v(15.15, 98) * mm, "end": v(15.15, 104.62) * mm});
            skCircle(sketch, "E83", {"center": v(0, 110) * mm, "radius": 6 * mm});
            skArc(sketch, "E84", {"start": v(15.15, 104.62) * mm, "mid": v(0, 119.62) * mm, "end": v(-14.85, 104.33) * mm});
            skLineSegment(sketch, "E85", {"start": v(-90, 0) * mm, "end": v(90, 0) * mm, "construction": true});
            skLineSegment(sketch, "E86.MirrorCS", {"start": v(33.15, -80) * mm, "end": v(15.15, -98) * mm});
            skLineSegment(sketch, "E87.MirrorCS", {"start": v(-32.85, -80) * mm, "end": v(-14.85, -98) * mm});
            skLineSegment(sketch, "E88.MirrorCS", {"start": v(-14.85, -98) * mm, "end": v(-14.85, -104.33) * mm});
            skLineSegment(sketch, "E89.MirrorCS", {"start": v(15.15, -98) * mm, "end": v(15.15, -104.62) * mm});
            skArc(sketch, "E90.MirrorCS", {"start": v(15.15, -104.62) * mm, "mid": v(0, -119.62) * mm, "end": v(-14.85, -104.33) * mm});
            skCircle(sketch, "E91.MirrorC", {"center": v(0, -110) * mm, "radius": 6 * mm});
            skLineSegment(sketch, "E92", {"start": v(0.15, 104.62) * mm, "end": v(0.15, 80) * mm, "construction": true});
            skLineSegment(sketch, "E93", {"start": v(0.15, -104.62) * mm, "end": v(0.15, -80) * mm, "construction": true});
            skSolve(sketch);
        }
        {
            var Q0;
            {var subQ0=sQuery(id+"F16.wireOp",EDGE,"E79");Q0=makeQuery(id+"F16.imprint","IMPRINT",FACE,{"disambiguationData":[TD([[makeQuery(id+"F16.imprint","IMPRINT",EDGE,{"derivedFrom":subQ0}),-1.0]])]});}
            var Q1;
            {var subQ0=sQuery(id+"F16.wireOp",EDGE,"E86.MirrorCS");Q1=makeQuery(id+"F16.imprint","IMPRINT",FACE,{"disambiguationData":[TD([[makeQuery(id+"F16.imprint","IMPRINT",EDGE,{"derivedFrom":subQ0}),-1.0]])]});}
            var Q2;
            Q2=makeQuery(id+"F16.imprint","IMPRINT",FACE,{"disambiguationData":[TD([[makeQuery(id+"F16.imprint","IMPRINT",EDGE,{"derivedFrom":makeQuery(id+"F1.opExtrude","CAP_EDGE",EDGE,{"disambiguationData":[OSD([sQuery(id+"F0.wireOp",EDGE,"E1.left")])],"isStart":true})}),-1.0]])]});
            var Q3;
            Q3=makeQuery(id+"F2.opExtrude","CAP_FACE",FACE,{"disambiguationData":[OSD([sQuery(id+"F0.wireOp",EDGE,"E12"),sQuery(id+"F0.wireOp",EDGE,"E13"),sQuery(id+"F0.wireOp",EDGE,"E14"),sQuery(id+"F0.wireOp",EDGE,"E15"),sQuery(id+"F0.wireOp",EDGE,"E17.filletArc"),sQuery(id+"F0.wireOp",EDGE,"E18.filletArc"),sQuery(id+"F0.wireOp",EDGE,"E19.filletArc"),sQuery(id+"F0.wireOp",EDGE,"E20.filletArc"),sQuery(id+"F0.wireOp",EDGE,"E25.0"),sQuery(id+"F0.wireOp",EDGE,"E25.1"),sQuery(id+"F0.wireOp",EDGE,"E25.2"),sQuery(id+"F0.wireOp",EDGE,"E25.3"),sQuery(id+"F0.wireOp",EDGE,"E25.4"),sQuery(id+"F0.wireOp",EDGE,"E25.5"),sQuery(id+"F0.wireOp",EDGE,"E25.6"),sQuery(id+"F0.wireOp",EDGE,"E25.7")])],"isStart":false});
            extrude(context, id + "F17", {"entities" : qUnion([Q0, Q1, Q2]), "endBound" : BoundingType.UP_TO_SURFACE, "endBoundEntityFace" : qUnion([Q3]), "depth" : 2.5 * mm});
        }
    });
